# Revit family: BLAUBERG-KOMFORT_Roto_EC_SE600
name_source: partatom
category: Mechanical Equipment
units: mm (PartAtom-declared; Revit-internal decimal feet)

## family parameters
Always vertical = Yes
Classification = None
Cut with Voids When Loaded = No
OmniClass Number = 23.75.35.14
OmniClass Title = Air Handling Units
Part Type = Normal
Room Calculation Point = No
Round Connector Dimension = Use Diameter
Shared = No
Work Plane-Based = No

## types (2) — shared parameters
B = 628 mm  [stored 2.06037 ft]
B1 = 183 mm
B2 = 183 mm
B3 = 128 mm  [stored 0.419948 ft]
BackFeetD = 20 mm  [stored 0.0656168 ft]
Casing Material = Painted Steel White
D = 200 mm  [stored 0.656168 ft]
Description = Air Handling Unit
Duct Connection Diameter = 200 mm  [stored 0.656168 ft]
Duct Connection Diameter Kitchen Hood = 125 mm  [stored 0.410105 ft]
ElBoxA = 160 mm  [stored 0.524934 ft]
ElBoxB = 292 mm  [stored 0.958005 ft]
ElConA = 393 mm  [stored 1.28937 ft]
ElConB = 386 mm  [stored 1.2664 ft]
Extract Air Filter = G4
Family Version = 1.0
Front Maintenance Zone Height = 800 mm  [stored 2.62467 ft]
Front Maintenance Zone Length = 816 mm  [stored 2.67717 ft]
Front Maintenance Zone Width = 771 mm  [stored 2.52953 ft]
H = 771 mm  [stored 2.52953 ft]
HDuctCon = 48 mm  [stored 0.15748 ft]
Heat Exchanger Material = aluminium
Heat Exchanger Type = rotary
Heat recovery efficiency (%) = 81..89
L = 816 mm  [stored 2.67717 ft]
L1 = 167 mm  [stored 0.5479 ft]
L2 = 167 mm  [stored 0.5479 ft]
L3 = 408 mm  [stored 1.33858 ft]
Load Classification = HVAC
Maintenance Zone Material = Maintenance Zone
Manufacturer = Blauberg
Maximum Air Flow = 670 m³/h
Maximum Unit Current Without Electric Heater = 3 A
Maximum Unit Power Without Electric Heater = 405 W
Metal Material = Metal Zinc
MountingPlateH = 100 mm  [stored 0.328084 ft]
Number of Poles = 1
Plastic Material = Polypropylene Black
Power Factor = 1
RPM (min-1) = 3230
SEC Class = A
ServiceDoorB = 20 mm  [stored 0.0656168 ft]
Sound Pressure Level at 3 m (dBA) = 35
Supply Air Filter = G4,F7
Transported Air Temperature (°C) = -25…+40
URL = https://blaubergventilatoren.de
Voltage = 230 V
dBFeets = 93 mm  [stored 0.305118 ft]
dLFeets = 27 mm  [stored 0.0885827 ft]

## per-type parameters (varying)
| type | Current | Heater power | Maximum Unit Current With Electric Heater | Power | Type Comments | Weight |
| KOMFORT Roto EC S 600 S21 | 3 A | 0 W | 3 A | 405 W | Air Handling Unit KOMFORT Roto EC S 600 S21 | 90.00 kg |
| KOMFORT Roto EC SE 600 S21 | 15 A | 2800 W | 15 A | 3205 W | Air Handling Unit KOMFORT Roto EC SE 600 S21 | 92.00 kg |

note: column(s) folded — value = type name in every type: Model

note: [stored X ft] marks values corroborated as IEEE doubles in the binary element streams (Revit-internal decimal feet)

## geometry (parser evidence)
native form markers: Sweep x5
no freeform markers — native parametric forms only
